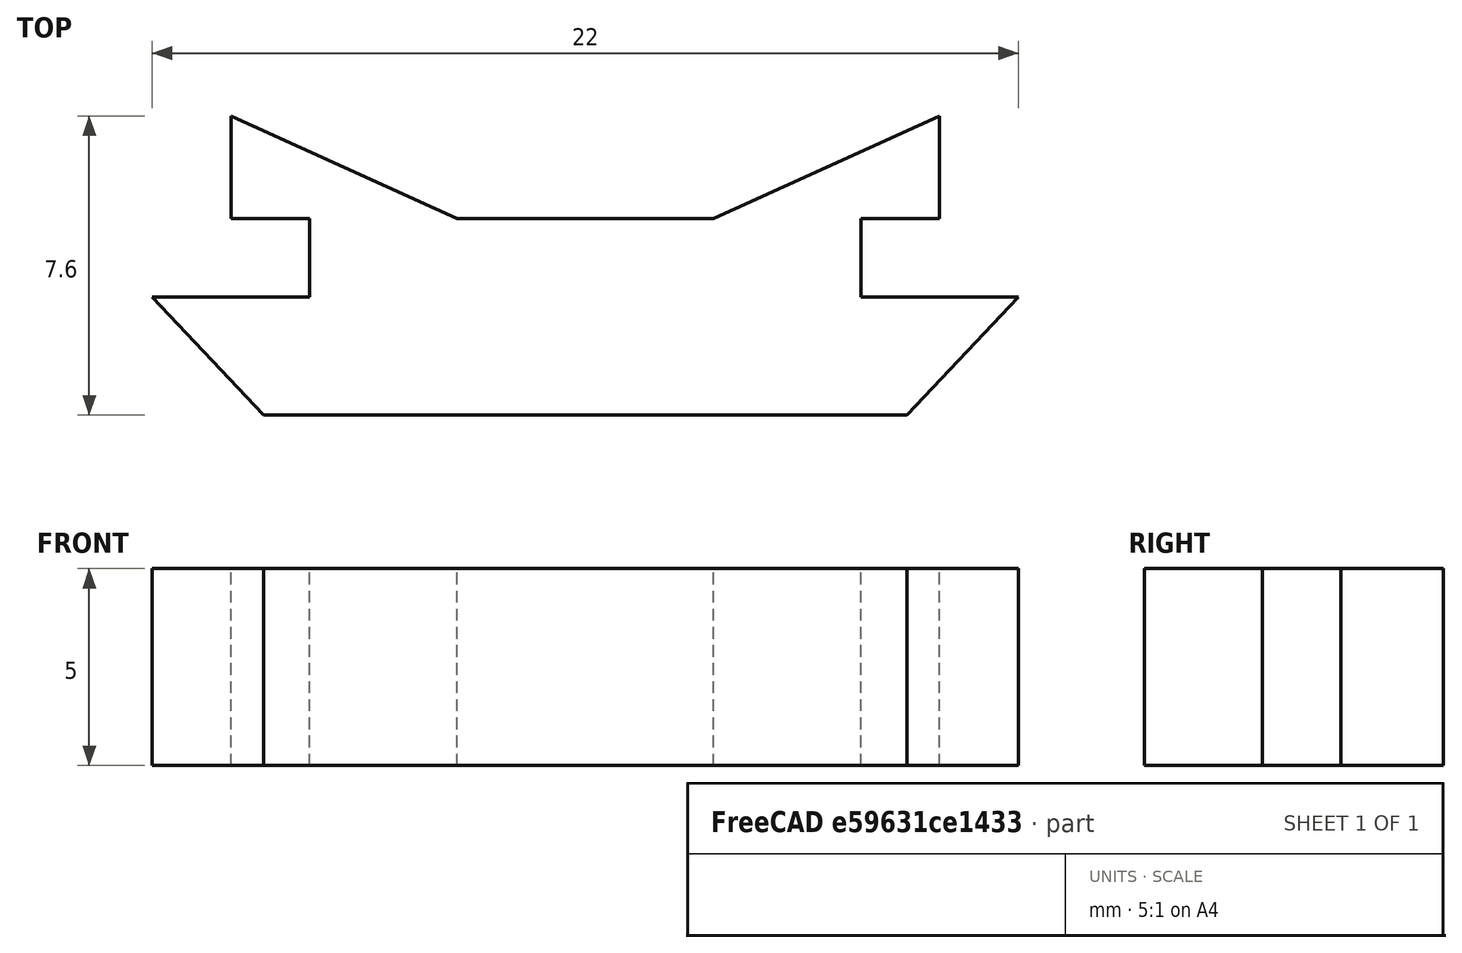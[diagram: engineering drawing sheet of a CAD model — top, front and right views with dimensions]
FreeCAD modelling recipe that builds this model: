
FCSTD DOCUMENT  (FreeCAD 0.19R)
Label: bike front light mount 3
License: All rights reserved
LicenseURL: http://en.wikipedia.org/wiki/All_rights_reserved
objects: Sketcher::SketchObject×1, PartDesign::Pad×1, PartDesign::Body×1
note: 4 computed .brp shape members not serialized (recipe doc carries the construction recipe); baked Part::Feature solids carry a one-line shape summary decoded from their .brp

FEATURE [Sketcher::SketchObject] Sketch
  FullyConstrained = false
  MapMode = 5
  Support = -> [XY_Plane]
  sketch-geometry (14):
    g0: LineSegment StartX=9 StartY=7.6 StartZ=0 EndX=9 EndY=5 EndZ=0
    g1: LineSegment StartX=9 StartY=5 StartZ=0 EndX=7 EndY=5 EndZ=0
    g2: LineSegment StartX=7 StartY=5 StartZ=0 EndX=7 EndY=3 EndZ=0
    g3: LineSegment StartX=7 StartY=3 StartZ=0 EndX=11 EndY=3 EndZ=0
    g4: LineSegment StartX=11 StartY=3 StartZ=0 EndX=8.16776 EndY=0 EndZ=0
    g5: LineSegment StartX=8.16776 StartY=0 StartZ=0 EndX=-8.16776 EndY=0 EndZ=0
    g6: LineSegment StartX=-8.16776 StartY=0 StartZ=0 EndX=-11 EndY=3 EndZ=0
    g7: LineSegment StartX=-11 StartY=3 StartZ=0 EndX=-7 EndY=3 EndZ=0
    g8: LineSegment StartX=-7 StartY=3 StartZ=0 EndX=-7 EndY=5 EndZ=0
    g9: LineSegment StartX=-7 StartY=5 StartZ=0 EndX=-9 EndY=5 EndZ=0
    g10: LineSegment StartX=-9 StartY=5 StartZ=0 EndX=-9 EndY=7.6 EndZ=0
    g11: LineSegment StartX=-3.25959 StartY=5 StartZ=0 EndX=3.25959 EndY=5 EndZ=0
    g12: LineSegment StartX=-9 StartY=7.6 StartZ=0 EndX=-3.25959 EndY=5 EndZ=0
    g13: LineSegment StartX=3.25959 StartY=5 StartZ=0 EndX=9 EndY=7.6 EndZ=0
  constraints (33):
    c: Vertical(g0)
    c: Coincident(g0,g1)
    c: Coincident(g1,g2)
    c: Vertical(g2)
    c: Coincident(g2,g3)
    c: Coincident(g3,g4)
    c: Coincident(g4,g5)
    c: Coincident(g5,g6)
    c: Coincident(g6,g7)
    c: Coincident(g7,g8)
    c: Coincident(g8,g9)
    c: Coincident(g9,g10)
    c: Symmetric(g10,g0,g-2)
    c: Symmetric(g9,g0,g-2)
    c: Symmetric(g1,g8,g-2)
    c: Symmetric(g2,g7,g-2)
    c: Symmetric(g3,g6,g-2)
    c: Symmetric(g5,g4,g-2)
    c: DistanceX(g10,g0) = 18
    c: DistanceY(g10,g10) = 2.6
    c: Horizontal(g9)
    c: DistanceY(g8,g8) = 2
    c: Horizontal(g7)
    c: DistanceX(g6,g3) = 22
    c: Symmetric(g5,g4,g-1)
    c: DistanceY(g6,g6) = 3
    c: DistanceX(g9,g9) = 2
    c: Horizontal(g8,g11)
    c: Coincident(g12,g10)
    c: Coincident(g12,g11)
    c: Coincident(g13,g11)
    c: Coincident(g13,g0)
    c: Symmetric(g11,g11,g-2)
FEATURE [PartDesign::Pad] Pad
  Direction = (1,1,1)
  Length = 5
  Length2 = 100
  Profile = -> Sketch
  Type = 0
FEATURE [PartDesign::Body] Body
  Group = -> [Sketch,Pad]
  Origin = -> Origin
  Tip = -> Pad
